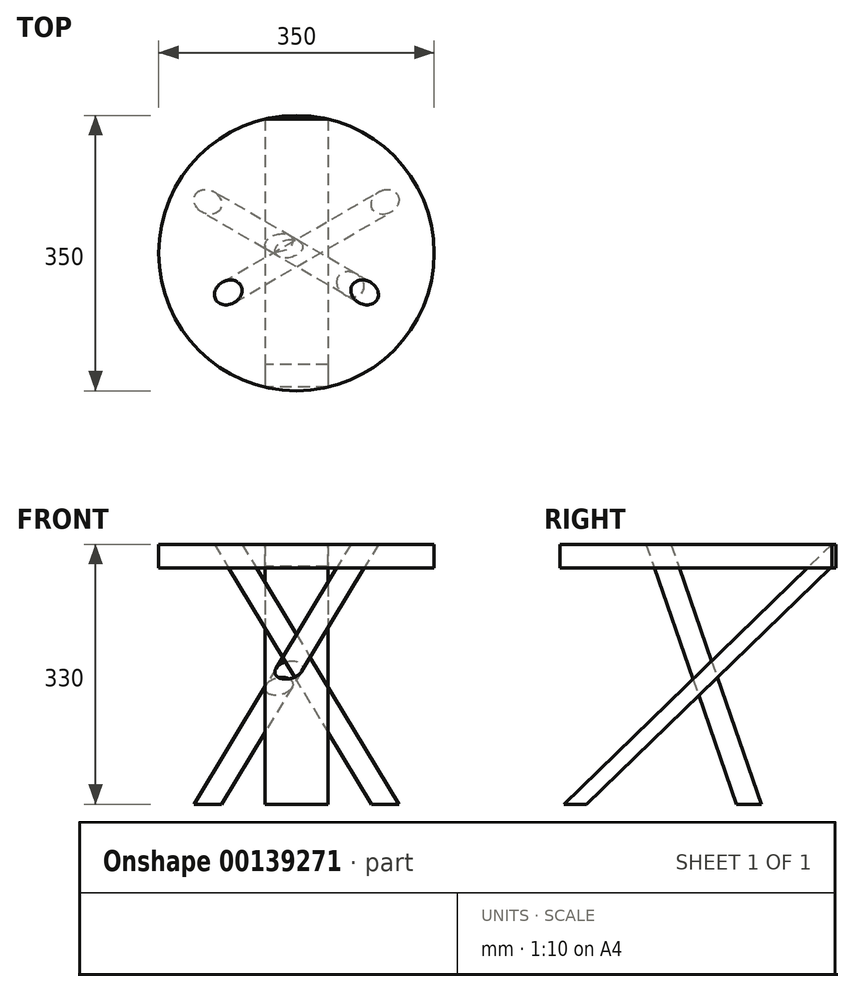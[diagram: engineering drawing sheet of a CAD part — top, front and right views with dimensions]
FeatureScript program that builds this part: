
annotation { "Feature Type Name" : "Feature", "Feature Type Description" : "" }
export const myFeature = defineFeature(function(context is Context, id is Id, definition is map)
    precondition{}
    {
        {
            var Q0;
            Q0=qCreatedBy(makeId("Top.planeOp"),FACE);
            var sketch = newSketch(context, id + "F0", { "sketchPlane" : qUnion([Q0])});
            skCircle(sketch, "E0", {"center": v(0, 0) * mm, "radius": 175 * mm});
            skLineSegment(sketch, "E1", {"start": v(0, 0) * mm, "end": v(0, 175) * mm, "construction": true});
            skLineSegment(sketch, "E2", {"start": v(151.55, 87.5) * mm, "end": v(-151.55, -87.5) * mm, "construction": true});
            skLineSegment(sketch, "E3", {"start": v(-151.55, 87.5) * mm, "end": v(151.55, -87.5) * mm, "construction": true});
            skLineSegment(sketch, "E4.bottom", {"start": v(-40, 170.37) * mm, "end": v(40, 170.37) * mm});
            skLineSegment(sketch, "E4.top", {"start": v(-40, -170.37) * mm, "end": v(40, -170.37) * mm});
            skLineSegment(sketch, "E4.left", {"start": v(-40, 170.37) * mm, "end": v(-40, -170.37) * mm});
            skLineSegment(sketch, "E4.right", {"start": v(40, 170.37) * mm, "end": v(40, -170.37) * mm});
            skLineSegment(sketch, "E5", {"start": v(-40, 150.37) * mm, "end": v(40, 150.37) * mm});
            skLineSegment(sketch, "E6", {"start": v(0, 0) * mm, "end": v(-121.63, 0) * mm, "construction": true});
            skLineSegment(sketch, "E7.MirrorCS", {"start": v(-40, -150.37) * mm, "end": v(40, -150.37) * mm});
            skCircle(sketch, "E8", {"center": v(0, 0) * mm, "radius": 170.37 * mm, "construction": true});
            skSolve(sketch);
        }
        {
            var Q0;
            {var subQ0=sQuery(id+"F0.wireOp",EDGE,"E4.left");var subQ4=makeQuery(id+"F0.imprint","INTERSECT",VERTEX,{"derivedFrom":[subQ0,sQuery(id+"F0.wireOp",EDGE,"E5")]});Q0=makeQuery(id+"F0.imprint","IMPRINT",FACE,{"disambiguationData":[TD([[makeQuery(id+"F0.imprint","IMPRINT",EDGE,{"disambiguationData":[TD([[subQ4,-1.0]])],"derivedFrom":subQ0}),-1.0]])]});}
            var Q1;
            {var subQ0=sQuery(id+"F0.wireOp",EDGE,"E5");Q1=makeQuery(id+"F0.imprint","IMPRINT",FACE,{"disambiguationData":[TD([[makeQuery(id+"F0.imprint","IMPRINT",EDGE,{"derivedFrom":subQ0}),-1.0]])]});}
            var Q2;
            {var subQ0=sQuery(id+"F0.wireOp",EDGE,"E4.bottom");Q2=makeQuery(id+"F0.imprint","IMPRINT",FACE,{"disambiguationData":[TD([[makeQuery(id+"F0.imprint","IMPRINT",EDGE,{"derivedFrom":subQ0}),-1.0]])]});}
            var Q3;
            {var subQ0=sQuery(id+"F0.wireOp",EDGE,"E4.bottom");Q3=makeQuery(id+"F0.imprint","IMPRINT",FACE,{"disambiguationData":[TD([[makeQuery(id+"F0.imprint","IMPRINT",EDGE,{"derivedFrom":subQ0}),1.0]])]});}
            var Q4;
            {var subQ0=sQuery(id+"F0.wireOp",EDGE,"E4.right");var subQ4=makeQuery(id+"F0.imprint","INTERSECT",VERTEX,{"derivedFrom":[subQ0,sQuery(id+"F0.wireOp",EDGE,"E5")]});Q4=makeQuery(id+"F0.imprint","IMPRINT",FACE,{"disambiguationData":[TD([[makeQuery(id+"F0.imprint","IMPRINT",EDGE,{"disambiguationData":[TD([[subQ4,-1.0]])],"derivedFrom":subQ0}),1.0]])]});}
            var Q5;
            {var subQ0=sQuery(id+"F0.wireOp",EDGE,"E4.top");Q5=makeQuery(id+"F0.imprint","IMPRINT",FACE,{"disambiguationData":[TD([[makeQuery(id+"F0.imprint","IMPRINT",EDGE,{"derivedFrom":subQ0}),1.0]])]});}
            var Q6;
            {var subQ0=sQuery(id+"F0.wireOp",EDGE,"E4.top");Q6=makeQuery(id+"F0.imprint","IMPRINT",FACE,{"disambiguationData":[TD([[makeQuery(id+"F0.imprint","IMPRINT",EDGE,{"derivedFrom":subQ0}),-1.0]])]});}
            extrude(context, id + "F1", {"entities" : qUnion([Q0, Q1, Q2, Q3, Q4, Q5, Q6]), "depth" : 30 * mm});
        }
        {
            var Q0;
            Q0=qCreatedBy(makeId("Front.planeOp"),FACE);
            var sketch = newSketch(context, id + "F2", { "sketchPlane" : qUnion([Q0])});
            skLineSegment(sketch, "E9.0", {"start": v(-175, 0) * mm, "end": v(175, 0) * mm});
            skLineSegment(sketch, "E10.bottom", {"start": v(-175, 0) * mm, "end": v(175, 0) * mm, "construction": true});
            skLineSegment(sketch, "E10.top", {"start": v(-175, -300) * mm, "end": v(175, -300) * mm, "construction": true});
            skLineSegment(sketch, "E10.left", {"start": v(-175, 0) * mm, "end": v(-175, -300) * mm, "construction": true});
            skLineSegment(sketch, "E10.right", {"start": v(175, 0) * mm, "end": v(175, -300) * mm, "construction": true});
            skLineSegment(sketch, "E11", {"start": v(0, 0) * mm, "end": v(0, -300) * mm, "construction": true});
            skSolve(sketch);
        }
        {
            var Q0;
            Q0=qCreatedBy(makeId("Right.planeOp"),FACE);
            var sketch = newSketch(context, id + "F3", { "sketchPlane" : qUnion([Q0])});
            skLineSegment(sketch, "E12", {"start": v(254.53, -300) * mm, "end": v(-254.53, -300) * mm, "construction": true});
            skLineSegment(sketch, "E13", {"start": v(-170.37, 0) * mm, "end": v(-170.37, -300) * mm, "construction": true});
            skLineSegment(sketch, "E14", {"start": v(170.37, 30) * mm, "end": v(-170.37, -300) * mm});
            skLineSegment(sketch, "E15.0", {"start": v(-175, 30) * mm, "end": v(175, 30) * mm});
            skLineSegment(sketch, "E16", {"start": v(170.37, 0) * mm, "end": v(170.37, 30) * mm});
            skLineSegment(sketch, "E17", {"start": v(170.37, 2.16) * mm, "end": v(-141.62, -300) * mm});
            skLineSegment(sketch, "E18", {"start": v(-141.62, -300) * mm, "end": v(-170.37, -300) * mm});
            skSolve(sketch);
        }
        {
            var Q0;
            {var subQ0=sQuery(id+"F3.wireOp",EDGE,"E14");Q0=makeQuery(id+"F3.imprint","IMPRINT",FACE,{"disambiguationData":[TD([[makeQuery(id+"F3.imprint","IMPRINT",EDGE,{"derivedFrom":subQ0}),1.0]])]});}
            extrude(context, id + "F4", {"entities" : qUnion([Q0]), "endBound" : BoundingType.SYMMETRIC, "depth" : 80 * mm});
        }
        {
            var Q0;
            Q0=sQuery(id+"F0.wireOp",EDGE,"E3");
            cPlane(context, id + "F5", {"entities" : qUnion([Q0]), "cplaneType" : CPlaneType.LINE_ANGLE, "offset" : 25 * mm, "angle" : 0 * degree, "width" : 150 * mm, "height" : 150 * mm});
        }
        {
            var Q0;
            Q0=qCreatedBy(id+"F5.planeOp",FACE);
            var sketch = newSketch(context, id + "F6", { "sketchPlane" : qUnion([Q0])});
            skLineSegment(sketch, "E19.0", {"start": v(151.55, 0) * mm, "end": v(-151.55, 0) * mm});
            skLineSegment(sketch, "E20", {"start": v(151.55, 0) * mm, "end": v(151.55, -348.94) * mm});
            skLineSegment(sketch, "E21", {"start": v(-151.55, 0) * mm, "end": v(-151.55, -346.12) * mm});
            skLineSegment(sketch, "E22.0", {"start": v(-175, 30) * mm, "end": v(175, 30) * mm});
            skLineSegment(sketch, "E23.0", {"start": v(151.55, -300) * mm, "end": v(-151.55, -300) * mm, "construction": true});
            skLineSegment(sketch, "E24", {"start": v(-100, 30) * mm, "end": v(130, -300) * mm});
            skLineSegment(sketch, "E25.0", {"start": v(0, 0) * mm, "end": v(0, -300) * mm, "construction": true});
            skSolve(sketch);
        }
        {
            var Q0;
            Q0=sQuery(id+"F6.wireOp",EDGE,"E24");
            var Q1;
            Q1=sQuery(id+"F6.wireOp",VERTEX,"E24.end");
            cPlane(context, id + "F7", {"entities" : qUnion([Q0, Q1]), "cplaneType" : CPlaneType.LINE_POINT, "offset" : 25 * mm, "width" : 150 * mm, "height" : 150 * mm});
        }
        {
            var Q0;
            Q0=qCreatedBy(id+"F7.planeOp",FACE);
            var sketch = newSketch(context, id + "F8", { "sketchPlane" : qUnion([Q0])});
            skCircle(sketch, "E26", {"center": v(53.06, 37.34) * mm, "radius": 15 * mm});
            skSolve(sketch);
        }
        {
            var Q0;
            Q0=makeQuery(id+"F8.imprint","IMPRINT",FACE,{"disambiguationData":[TD([[makeQuery(id+"F8.imprint","IMPRINT",EDGE,{"derivedFrom":sQuery(id+"F8.wireOp",EDGE,"E26")}),1.0]])]});
            extrude(context, id + "F9", {"entities" : qUnion([Q0]), "operationType" : NewBodyOperationType.REMOVE, "endBound" : BoundingType.THROUGH_ALL, "oppositeDirection" : true, "depth" : 25 * mm});
        }
        {
            var Q0;
            Q0 = qSketchRegion(id + "F8", true);
            extrude(context, id + "F10", {"entities" : qUnion([Q0]), "operationType" : NewBodyOperationType.REMOVE, "endBound" : BoundingType.THROUGH_ALL, "oppositeDirection" : true, "depth" : 25 * mm});
        }
        {
            var Q0;
            Q0=makeQuery(id+"F8.imprint","IMPRINT",FACE,{"disambiguationData":[TD([[makeQuery(id+"F8.imprint","IMPRINT",EDGE,{"derivedFrom":sQuery(id+"F8.wireOp",EDGE,"E26")}),1.0]])]});
            extrude(context, id + "F11", {"entities" : qUnion([Q0]), "endBound" : BoundingType.THROUGH_ALL, "oppositeDirection" : true, "depth" : 25 * mm, "hasSecondDirection" : true, "secondDirectionOppositeDirection" : false, "secondDirectionDepth" : 50 * mm});
        }
        {
            var Q0;
            Q0=makeQuery(id+"F4.opExtrude","SWEPT_FACE",FACE,{"disambiguationData":[OSD([sQuery(id+"F3.wireOp",EDGE,"E18")])]});
            var sketch = newSketch(context, id + "F12", { "sketchPlane" : qUnion([Q0])});
            skLineSegment(sketch, "E27.bottom", {"start": v(40, 170.37) * mm, "end": v(-160, 170.37) * mm});
            skLineSegment(sketch, "E27.top", {"start": v(40, -119.63) * mm, "end": v(-160, -119.63) * mm});
            skLineSegment(sketch, "E27.left", {"start": v(40, 170.37) * mm, "end": v(40, -119.63) * mm});
            skLineSegment(sketch, "E27.right", {"start": v(-160, 170.37) * mm, "end": v(-160, -119.63) * mm});
            skSolve(sketch);
        }
        {
            var Q0;
            {var subQ3=sQuery(id+"F12.wireOp",EDGE,"E27.top");Q0=makeQuery(id+"F12.imprint","IMPRINT",FACE,{"disambiguationData":[TD([[makeQuery(id+"F12.imprint","IMPRINT",EDGE,{"derivedFrom":subQ3}),-1.0]])]});}
            extrude(context, id + "F13", {"entities" : qUnion([Q0]), "operationType" : NewBodyOperationType.REMOVE, "endBound" : BoundingType.THROUGH_ALL, "depth" : 25 * mm});
        }
        {
            var Q0;
            Q0=makeQuery(id+"F1.opExtrude","CAP_FACE",FACE,{"disambiguationData":[OSD([sQuery(id+"F0.wireOp",EDGE,"E0")])],"isStart":false});
            var sketch = newSketch(context, id + "F14", { "sketchPlane" : qUnion([Q0])});
            skLineSegment(sketch, "E28.bottom", {"start": v(212.5, -150) * mm, "end": v(-212.5, -150) * mm});
            skLineSegment(sketch, "E28.top", {"start": v(212.5, 150) * mm, "end": v(-212.5, 150) * mm});
            skLineSegment(sketch, "E28.left", {"start": v(212.5, -150) * mm, "end": v(212.5, 150) * mm});
            skLineSegment(sketch, "E28.right", {"start": v(-212.5, -150) * mm, "end": v(-212.5, 150) * mm});
            skPoint(sketch, "E28.middle", {"position": v(0, 0) * mm});
            skSolve(sketch);
        }
        {
            var Q0;
            Q0 = qSketchRegion(id + "F14", true);
            extrude(context, id + "F15", {"entities" : qUnion([Q0]), "operationType" : NewBodyOperationType.REMOVE, "endBound" : BoundingType.THROUGH_ALL, "depth" : 25 * mm});
        }
        {
            var Q0;
            Q0=makeQuery(id+"F1.opExtrude","CAP_FACE",FACE,{"disambiguationData":[OSD([sQuery(id+"F0.wireOp",EDGE,"E0")])],"isStart":false});
            var sketch = newSketch(context, id + "F16", { "sketchPlane" : qUnion([Q0])});
            skPoint(sketch, "E29.0", {"position": v(-112.58, 65) * mm});
            skLineSegment(sketch, "E30.0", {"start": v(151.55, 87.5) * mm, "end": v(-151.55, -87.5) * mm, "construction": true});
            skSolve(sketch);
        }
        {
            var Q0;
            {var subQ0=sQuery(id+"F0.wireOp",EDGE,"E0");Q0=makeQuery(id+"F16.imprint","IMPRINT",FACE,{"disambiguationData":[TD([[makeQuery(id+"F16.imprint","IMPRINT",EDGE,{"derivedFrom":makeQuery(id+"F1.opExtrude","CAP_EDGE",EDGE,{"disambiguationData":[OSD([subQ0])],"isStart":false})}),1.0]])]});}
            var Q1;
            Q1=sQuery(id+"F16.wireOp",EDGE,"E30.0");
            cPlane(context, id + "F17", {"entities" : qUnion([Q0, Q1]), "cplaneType" : CPlaneType.LINE_ANGLE, "offset" : 25 * mm, "angle" : 90 * degree, "width" : 150 * mm, "height" : 150 * mm});
        }
        {
            var Q0;
            Q0=qCreatedBy(id+"F17.planeOp",FACE);
            var sketch = newSketch(context, id + "F18", { "sketchPlane" : qUnion([Q0])});
            skLineSegment(sketch, "E31.0", {"start": v(-75.78, -300) * mm, "end": v(75.78, -300) * mm, "construction": true});
            skLineSegment(sketch, "E32.0", {"start": v(175, 30) * mm, "end": v(-175, 30) * mm, "construction": true});
            skLineSegment(sketch, "E33.0", {"start": v(0, 0) * mm, "end": v(0, -300) * mm, "construction": true});
            skLineSegment(sketch, "E34", {"start": v(-100, 30) * mm, "end": v(130, -300) * mm});
            skLineSegment(sketch, "E35", {"start": v(-100, 30) * mm, "end": v(-122.87, 62.82) * mm});
            skLineSegment(sketch, "E36", {"start": v(130, -300) * mm, "end": v(158.59, -341.02) * mm});
            skSolve(sketch);
        }
        {
            var Q0;
            Q0=sQuery(id+"F18.wireOp",EDGE,"E36");
            var Q1;
            Q1=sQuery(id+"F18.wireOp",VERTEX,"E36.end");
            cPlane(context, id + "F19", {"entities" : qUnion([Q0, Q1]), "cplaneType" : CPlaneType.LINE_POINT, "offset" : 25 * mm, "width" : 150 * mm, "height" : 150 * mm});
        }
        {
            var Q0;
            Q0=qCreatedBy(id+"F19.planeOp",FACE);
            var sketch = newSketch(context, id + "F20", { "sketchPlane" : qUnion([Q0])});
            skCircle(sketch, "E37", {"center": v(-53.06, 37.34) * mm, "radius": 15 * mm});
            skSolve(sketch);
        }
        {
            var Q0;
            Q0=makeQuery(id+"F20.imprint","IMPRINT",FACE,{"disambiguationData":[TD([[makeQuery(id+"F20.imprint","IMPRINT",EDGE,{"derivedFrom":sQuery(id+"F20.wireOp",EDGE,"E37")}),1.0]])]});
            var Q1;
            Q1=makeQuery(id+"F1.opExtrude","CAP_FACE",FACE,{"disambiguationData":[OSD([sQuery(id+"F0.wireOp",EDGE,"E0")])],"isStart":false});
            extrude(context, id + "F21", {"entities" : qUnion([Q0]), "endBound" : BoundingType.UP_TO_SURFACE, "oppositeDirection" : true, "endBoundEntityFace" : qUnion([Q1]), "depth" : 25 * mm});
        }
        {
            var Q0;
            Q0=makeQuery(id+"F4.opExtrude","SWEPT_FACE",FACE,{"disambiguationData":[OSD([sQuery(id+"F3.wireOp",EDGE,"E18")])]});
            var sketch = newSketch(context, id + "F22", { "sketchPlane" : qUnion([Q0])});
            skLineSegment(sketch, "E38.bottom", {"start": v(-40, 170.37) * mm, "end": v(260, 170.37) * mm});
            skLineSegment(sketch, "E38.top", {"start": v(-40, -129.63) * mm, "end": v(260, -129.63) * mm});
            skLineSegment(sketch, "E38.left", {"start": v(-40, 170.37) * mm, "end": v(-40, -129.63) * mm});
            skLineSegment(sketch, "E38.right", {"start": v(260, 170.37) * mm, "end": v(260, -129.63) * mm});
            skSolve(sketch);
        }
        {
            var Q0;
            {var subQ3=sQuery(id+"F22.wireOp",EDGE,"E38.top");Q0=makeQuery(id+"F22.imprint","IMPRINT",FACE,{"disambiguationData":[TD([[makeQuery(id+"F22.imprint","IMPRINT",EDGE,{"derivedFrom":subQ3}),1.0]])]});}
            extrude(context, id + "F23", {"entities" : qUnion([Q0]), "operationType" : NewBodyOperationType.REMOVE, "endBound" : BoundingType.THROUGH_ALL, "depth" : 25 * mm});
        }
    });
